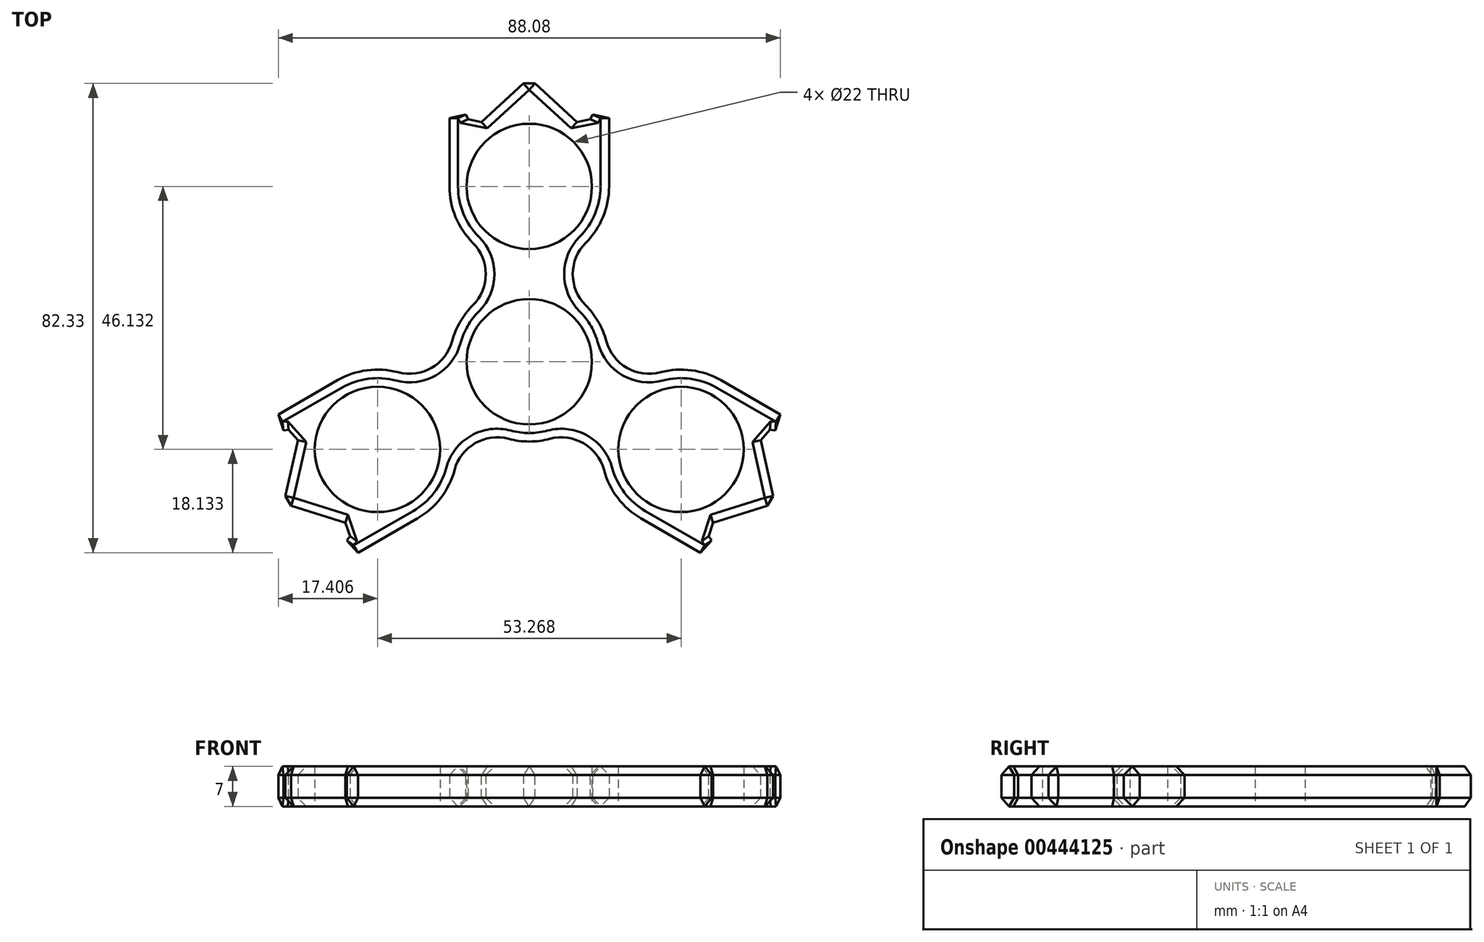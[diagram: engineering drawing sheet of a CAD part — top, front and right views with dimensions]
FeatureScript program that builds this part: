
annotation { "Feature Type Name" : "Feature", "Feature Type Description" : "" }
export const myFeature = defineFeature(function(context is Context, id is Id, definition is map)
    precondition{}
    {
        {
            var Q0;
            Q0=qCreatedBy(makeId("Top.planeOp"),FACE);
            var sketch = newSketch(context, id + "F0", { "sketchPlane" : qUnion([Q0])});
            skCircle(sketch, "E0", {"center": v(0, 0) * mm, "radius": 11 * mm});
            skArc(sketch, "E1.0", {"start": v(-9.9, 9.9) * mm, "mid": v(-12.12, 7) * mm, "end": v(-13.52, 3.62) * mm});
            skCircle(sketch, "E2", {"center": v(0, 30.75) * mm, "radius": 11 * mm});
            skArc(sketch, "E3.0", {"start": v(9.9, 20.85) * mm, "mid": v(12.93, 25.4) * mm, "end": v(14, 30.75) * mm});
            skPoint(sketch, "E4.end.orphan", {"position": v(-14, 0) * mm});
            skPoint(sketch, "E5.MirrorCS.end.orphan", {"position": v(14, 0) * mm});
            skArc(sketch, "E6", {"start": v(9.9, 20.85) * mm, "mid": v(7.63, 15.38) * mm, "end": v(9.9, 9.9) * mm});
            skPoint(sketch, "E7", {"position": v(9.9, 20.85) * mm});
            skPoint(sketch, "E8.MirrorP", {"position": v(-9.9, 40.65) * mm});
            skPoint(sketch, "E9.MirrorP", {"position": v(9.9, 40.65) * mm});
            skLineSegment(sketch, "E10", {"start": v(0, 44.75) * mm, "end": v(0, 49.75) * mm});
            skPoint(sketch, "E10.endSnap0", {"position": v(0, 44.75) * mm});
            skLineSegment(sketch, "E11", {"start": v(-14, 30.75) * mm, "end": v(-14, 49.75) * mm});
            skLineSegment(sketch, "E12", {"start": v(-14, 49.75) * mm, "end": v(-9.9, 40.65) * mm});
            skLineSegment(sketch, "E13", {"start": v(-9.9, 40.65) * mm, "end": v(0, 49.75) * mm});
            skLineSegment(sketch, "E14.MirrorCS", {"start": v(9.9, 40.65) * mm, "end": v(0, 49.75) * mm});
            skLineSegment(sketch, "E15.MirrorCS", {"start": v(14, 49.75) * mm, "end": v(9.9, 40.65) * mm});
            skLineSegment(sketch, "E16.MirrorCS", {"start": v(14, 30.75) * mm, "end": v(14, 49.75) * mm});
            skArc(sketch, "E17", {"start": v(-9.9, 20.85) * mm, "mid": v(-7.63, 15.38) * mm, "end": v(-9.9, 9.9) * mm});
            skArc(sketch, "E18.1.0", {"start": v(-13.11, -19) * mm, "mid": v(-9.5, -14.3) * mm, "end": v(-3.62, -13.52) * mm});
            skCircle(sketch, "E18.1.1", {"center": v(-26.63, -15.38) * mm, "radius": 11 * mm});
            skArc(sketch, "E18.1.2", {"start": v(-23.01, -1.85) * mm, "mid": v(-17.13, -1.08) * mm, "end": v(-13.52, 3.62) * mm});
            skArc(sketch, "E18.1.3", {"start": v(-23.01, -1.85) * mm, "mid": v(-28.46, -1.5) * mm, "end": v(-33.63, -3.25) * mm});
            skLineSegment(sketch, "E18.1.4", {"start": v(-33.63, -3.25) * mm, "end": v(-50.09, -12.75) * mm});
            skLineSegment(sketch, "E18.1.5", {"start": v(-50.09, -12.75) * mm, "end": v(-40.16, -11.75) * mm});
            skLineSegment(sketch, "E18.1.6", {"start": v(-40.16, -11.75) * mm, "end": v(-43.09, -24.88) * mm});
            skLineSegment(sketch, "E18.1.7", {"start": v(-30.26, -28.9) * mm, "end": v(-43.09, -24.88) * mm});
            skLineSegment(sketch, "E18.1.8", {"start": v(-36.09, -37) * mm, "end": v(-30.26, -28.9) * mm});
            skLineSegment(sketch, "E18.1.9", {"start": v(-19.63, -27.5) * mm, "end": v(-36.09, -37) * mm});
            skArc(sketch, "E18.2.0", {"start": v(23.01, -1.85) * mm, "mid": v(17.13, -1.08) * mm, "end": v(13.52, 3.62) * mm});
            skCircle(sketch, "E18.2.1", {"center": v(26.63, -15.38) * mm, "radius": 11 * mm});
            skArc(sketch, "E18.2.2", {"start": v(13.11, -19) * mm, "mid": v(9.5, -14.3) * mm, "end": v(3.62, -13.52) * mm});
            skArc(sketch, "E18.2.3", {"start": v(13.11, -19) * mm, "mid": v(15.53, -23.9) * mm, "end": v(19.63, -27.5) * mm});
            skLineSegment(sketch, "E18.2.4", {"start": v(19.63, -27.5) * mm, "end": v(36.09, -37) * mm});
            skLineSegment(sketch, "E18.2.5", {"start": v(36.09, -37) * mm, "end": v(30.26, -28.9) * mm});
            skLineSegment(sketch, "E18.2.6", {"start": v(30.26, -28.9) * mm, "end": v(43.09, -24.88) * mm});
            skLineSegment(sketch, "E18.2.7", {"start": v(40.16, -11.75) * mm, "end": v(43.09, -24.88) * mm});
            skLineSegment(sketch, "E18.2.8", {"start": v(50.09, -12.75) * mm, "end": v(40.16, -11.75) * mm});
            skLineSegment(sketch, "E18.2.9", {"start": v(33.63, -3.25) * mm, "end": v(50.09, -12.75) * mm});
            skArc(sketch, "E19.trimOffspring", {"start": v(-3.62, -13.52) * mm, "mid": v(0, -14) * mm, "end": v(3.62, -13.52) * mm});
            skArc(sketch, "E20.trimOffspring", {"start": v(13.52, 3.62) * mm, "mid": v(12.12, 7) * mm, "end": v(9.9, 9.9) * mm});
            skArc(sketch, "E21.trimOffspring", {"start": v(-14, 30.75) * mm, "mid": v(-12.93, 25.4) * mm, "end": v(-9.9, 20.85) * mm});
            skArc(sketch, "E22.trimOffspring", {"start": v(-9.03, 41.45) * mm, "mid": v(-9.47, 41.06) * mm, "end": v(-9.9, 40.65) * mm});
            skArc(sketch, "E23.trimOffspring", {"start": v(9.9, 40.65) * mm, "mid": v(9.47, 41.06) * mm, "end": v(9.03, 41.45) * mm});
            skArc(sketch, "E24.trimOffspring", {"start": v(33.63, -3.25) * mm, "mid": v(28.46, -1.5) * mm, "end": v(23.01, -1.85) * mm});
            skArc(sketch, "E25.trimOffspring", {"start": v(40.41, -12.9) * mm, "mid": v(40.3, -12.33) * mm, "end": v(40.16, -11.75) * mm});
            skArc(sketch, "E26.trimOffspring", {"start": v(30.26, -28.9) * mm, "mid": v(30.82, -28.74) * mm, "end": v(31.38, -28.55) * mm});
            skArc(sketch, "E27.trimOffspring", {"start": v(-31.38, -28.55) * mm, "mid": v(-30.82, -28.74) * mm, "end": v(-30.26, -28.9) * mm});
            skArc(sketch, "E28.trimOffspring", {"start": v(-40.16, -11.75) * mm, "mid": v(-40.3, -12.33) * mm, "end": v(-40.41, -12.9) * mm});
            skArc(sketch, "E29.trimOffspring", {"start": v(-19.63, -27.5) * mm, "mid": v(-15.53, -23.9) * mm, "end": v(-13.11, -19) * mm});
            skSolve(sketch);
        }
        {
            var Q0;
            Q0=makeQuery(id+"F0.imprint","IMPRINT",FACE,{"disambiguationData":[TD([[makeQuery(id+"F0.imprint","IMPRINT",EDGE,{"derivedFrom":sQuery(id+"F0.wireOp",EDGE,"E0")}),-1.0]])]});
            extrude(context, id + "F1", {"entities" : qUnion([Q0]), "endBound" : BoundingType.SYMMETRIC, "depth" : 7 * mm});
        }
        {
            var Q0;
            Q0=makeQuery(id+"F1.opExtrude","SWEPT_FACE",FACE,{"disambiguationData":[OSD([sQuery(id+"F0.wireOp",EDGE,"E18.1.4")])]});
            var Q1;
            Q1=makeQuery(id+"F1.opExtrude","SWEPT_FACE",FACE,{"disambiguationData":[OSD([sQuery(id+"F0.wireOp",EDGE,"E18.1.3")])]});
            var Q2;
            Q2=makeQuery(id+"F1.opExtrude","SWEPT_FACE",FACE,{"disambiguationData":[OSD([sQuery(id+"F0.wireOp",EDGE,"E18.1.2")])]});
            var Q3;
            Q3=makeQuery(id+"F1.opExtrude","SWEPT_FACE",FACE,{"disambiguationData":[OSD([sQuery(id+"F0.wireOp",EDGE,"E1.0")])]});
            var Q4;
            Q4=makeQuery(id+"F1.opExtrude","SWEPT_FACE",FACE,{"disambiguationData":[OSD([sQuery(id+"F0.wireOp",EDGE,"E17")])]});
            var Q5;
            Q5=makeQuery(id+"F1.opExtrude","SWEPT_FACE",FACE,{"disambiguationData":[OSD([sQuery(id+"F0.wireOp",EDGE,"E21.trimOffspring")])]});
            var Q6;
            Q6=makeQuery(id+"F1.opExtrude","SWEPT_FACE",FACE,{"disambiguationData":[OSD([sQuery(id+"F0.wireOp",EDGE,"E13")])]});
            var Q7;
            Q7=makeQuery(id+"F1.opExtrude","SWEPT_FACE",FACE,{"disambiguationData":[OSD([sQuery(id+"F0.wireOp",EDGE,"E14.MirrorCS")])]});
            var Q8;
            Q8=makeQuery(id+"F1.opExtrude","SWEPT_FACE",FACE,{"disambiguationData":[OSD([sQuery(id+"F0.wireOp",EDGE,"E15.MirrorCS")])]});
            var Q9;
            Q9=makeQuery(id+"F1.opExtrude","SWEPT_FACE",FACE,{"disambiguationData":[OSD([sQuery(id+"F0.wireOp",EDGE,"E18.1.5")])]});
            var Q10;
            Q10=makeQuery(id+"F1.opExtrude","SWEPT_FACE",FACE,{"disambiguationData":[OSD([sQuery(id+"F0.wireOp",EDGE,"E18.1.6")])]});
            var Q11;
            Q11=makeQuery(id+"F1.opExtrude","SWEPT_FACE",FACE,{"disambiguationData":[OSD([sQuery(id+"F0.wireOp",EDGE,"E18.1.7")])]});
            var Q12;
            Q12=makeQuery(id+"F1.opExtrude","SWEPT_FACE",FACE,{"disambiguationData":[OSD([sQuery(id+"F0.wireOp",EDGE,"E18.1.8")])]});
            var Q13;
            Q13=makeQuery(id+"F1.opExtrude","SWEPT_FACE",FACE,{"disambiguationData":[OSD([sQuery(id+"F0.wireOp",EDGE,"E29.trimOffspring")])]});
            var Q14;
            Q14=makeQuery(id+"F1.opExtrude","SWEPT_FACE",FACE,{"disambiguationData":[OSD([sQuery(id+"F0.wireOp",EDGE,"E18.1.0")])]});
            var Q15;
            Q15=makeQuery(id+"F1.opExtrude","SWEPT_FACE",FACE,{"disambiguationData":[OSD([sQuery(id+"F0.wireOp",EDGE,"E19.trimOffspring")])]});
            var Q16;
            Q16=makeQuery(id+"F1.opExtrude","SWEPT_FACE",FACE,{"disambiguationData":[OSD([sQuery(id+"F0.wireOp",EDGE,"E18.2.2")])]});
            var Q17;
            Q17=makeQuery(id+"F1.opExtrude","SWEPT_FACE",FACE,{"disambiguationData":[OSD([sQuery(id+"F0.wireOp",EDGE,"E18.2.3")])]});
            var Q18;
            Q18=makeQuery(id+"F1.opExtrude","SWEPT_FACE",FACE,{"disambiguationData":[OSD([sQuery(id+"F0.wireOp",EDGE,"E18.2.4")])]});
            var Q19;
            Q19=makeQuery(id+"F1.opExtrude","SWEPT_FACE",FACE,{"disambiguationData":[OSD([sQuery(id+"F0.wireOp",EDGE,"E18.2.6")])]});
            var Q20;
            Q20=makeQuery(id+"F1.opExtrude","SWEPT_FACE",FACE,{"disambiguationData":[OSD([sQuery(id+"F0.wireOp",EDGE,"E18.2.7")])]});
            var Q21;
            Q21=makeQuery(id+"F1.opExtrude","SWEPT_FACE",FACE,{"disambiguationData":[OSD([sQuery(id+"F0.wireOp",EDGE,"E18.2.8")])]});
            var Q22;
            Q22=makeQuery(id+"F1.opExtrude","SWEPT_FACE",FACE,{"disambiguationData":[OSD([sQuery(id+"F0.wireOp",EDGE,"E18.2.5")])]});
            var Q23;
            Q23=makeQuery(id+"F1.opExtrude","SWEPT_FACE",FACE,{"disambiguationData":[OSD([sQuery(id+"F0.wireOp",EDGE,"E18.2.9")])]});
            var Q24;
            Q24=makeQuery(id+"F1.opExtrude","SWEPT_FACE",FACE,{"disambiguationData":[OSD([sQuery(id+"F0.wireOp",EDGE,"E24.trimOffspring")])]});
            var Q25;
            Q25=makeQuery(id+"F1.opExtrude","SWEPT_FACE",FACE,{"disambiguationData":[OSD([sQuery(id+"F0.wireOp",EDGE,"E18.2.0")])]});
            var Q26;
            Q26=makeQuery(id+"F1.opExtrude","SWEPT_FACE",FACE,{"disambiguationData":[OSD([sQuery(id+"F0.wireOp",EDGE,"E20.trimOffspring")])]});
            var Q27;
            Q27=makeQuery(id+"F1.opExtrude","SWEPT_FACE",FACE,{"disambiguationData":[OSD([sQuery(id+"F0.wireOp",EDGE,"E6")])]});
            var Q28;
            Q28=makeQuery(id+"F1.opExtrude","SWEPT_FACE",FACE,{"disambiguationData":[OSD([sQuery(id+"F0.wireOp",EDGE,"E3.0")])]});
            var Q29;
            Q29=makeQuery(id+"F1.opExtrude","SWEPT_FACE",FACE,{"disambiguationData":[OSD([sQuery(id+"F0.wireOp",EDGE,"E16.MirrorCS")])]});
            var Q30;
            Q30=makeQuery(id+"F1.opExtrude","SWEPT_FACE",FACE,{"disambiguationData":[OSD([sQuery(id+"F0.wireOp",EDGE,"E12")])]});
            var Q31;
            Q31=makeQuery(id+"F1.opExtrude","SWEPT_FACE",FACE,{"disambiguationData":[OSD([sQuery(id+"F0.wireOp",EDGE,"E18.1.9")])]});
            var Q32;
            Q32=makeQuery(id+"F1.opExtrude","SWEPT_FACE",FACE,{"disambiguationData":[OSD([sQuery(id+"F0.wireOp",EDGE,"E11")])]});
            chamfer(context, id + "F2", {"entities" : qUnion([Q0, Q1, Q2, Q3, Q4, Q5, Q6, Q7, Q8, Q9, Q10, Q11, Q12, Q13, Q14, Q15, Q16, Q17, Q18, Q19, Q20, Q21, Q22, Q23, Q24, Q25, Q26, Q27, Q28, Q29, Q30, Q31, Q32]), "width" : 1.5 * mm, "tangentPropagation" : true});
        }
    });
